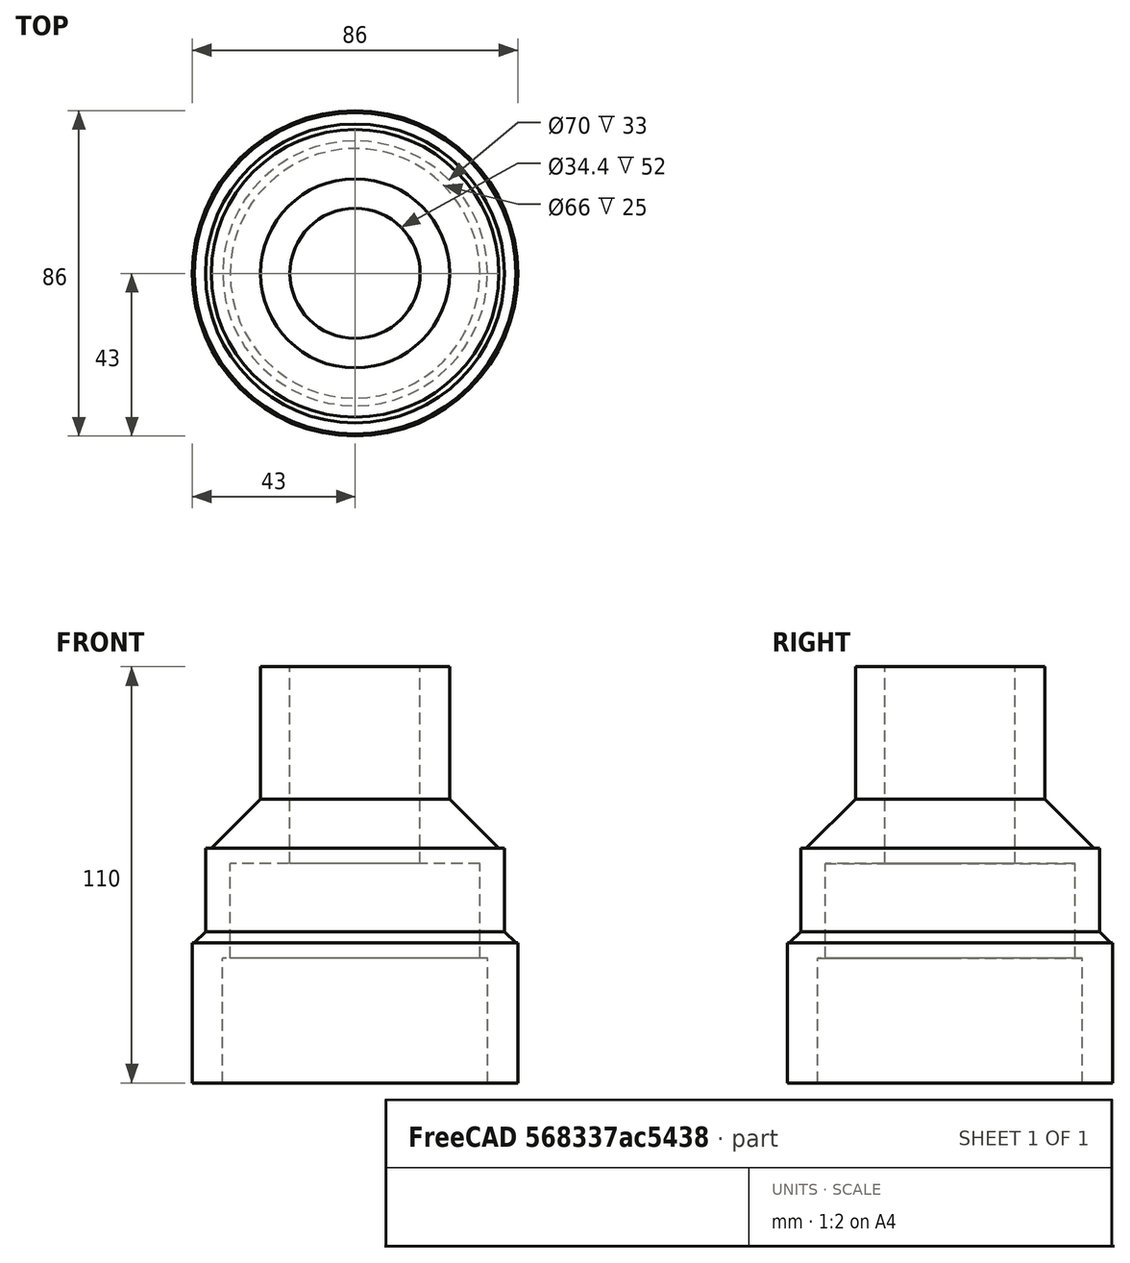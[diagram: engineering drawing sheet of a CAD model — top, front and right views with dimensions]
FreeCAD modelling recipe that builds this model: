
FCSTD DOCUMENT  (FreeCAD 0.14R3702 (Git))
Label: canon-microscope
License: CC-BY 3.0
LicenseURL: http://creativecommons.org/licenses/by/3.0/
objects: Part::Cylinder×6, Part::Cut×3, Part::Fuse×2, Part::Chamfer×2
note: 13 computed .brp shape members not serialized (recipe doc carries the construction recipe); baked Part::Feature solids carry a one-line shape summary decoded from their .brp

FEATURE [Part::Cylinder] Cylinder
  Angle = 360
  Height = 37
  Radius = 43
FEATURE [Part::Cylinder] Cylinder001
  Angle = 360
  Height = 26
  Placement = pos=(0,0,36) rot=(0,0,1;0rad)
  Radius = 39.5
FEATURE [Part::Fuse] Fusion003
  Base = -> Cylinder
  Tool = -> Cylinder001
FEATURE [Part::Cylinder] Cylinder003
  Angle = 360
  Height = 49
  Placement = pos=(0,0,61) rot=(0,0,1;0rad)
  Radius = 25
FEATURE [Part::Fuse] Fusion002
  Base = -> Cylinder003
  Placement = pos=(0,0,4) rot=(0,0,1;0rad)
  Tool = -> Fusion003
FEATURE [Part::Cylinder] Cylinder004
  Angle = 360
  Height = 63
  Placement = pos=(0,0,61) rot=(0,0,1;0rad)
  Radius = 17.2
FEATURE [Part::Cylinder] Cylinder005
  Angle = 360
  Height = 37
  Radius = 35
FEATURE [Part::Cylinder] Cylinder006
  Angle = 360
  Height = 26
  Placement = pos=(0,0,36) rot=(0,0,1;0rad)
  Radius = 33
FEATURE [Part::Cut] Cut
  Base = -> Fusion002
  Tool = -> Cylinder004
FEATURE [Part::Cut] Cut001
  Base = -> Cut
  Tool = -> Cylinder005
FEATURE [Part::Cut] Cut002
  Base = -> Cut001
  Tool = -> Cylinder006
FEATURE [Part::Chamfer] Chamfer
  Base = -> Cut002
  Edges = 1 edges r=13: [Edge4]
FEATURE [Part::Chamfer] Chamfer001
  Base = -> Chamfer
  Edges = 1 edges r=3: [Edge11]
